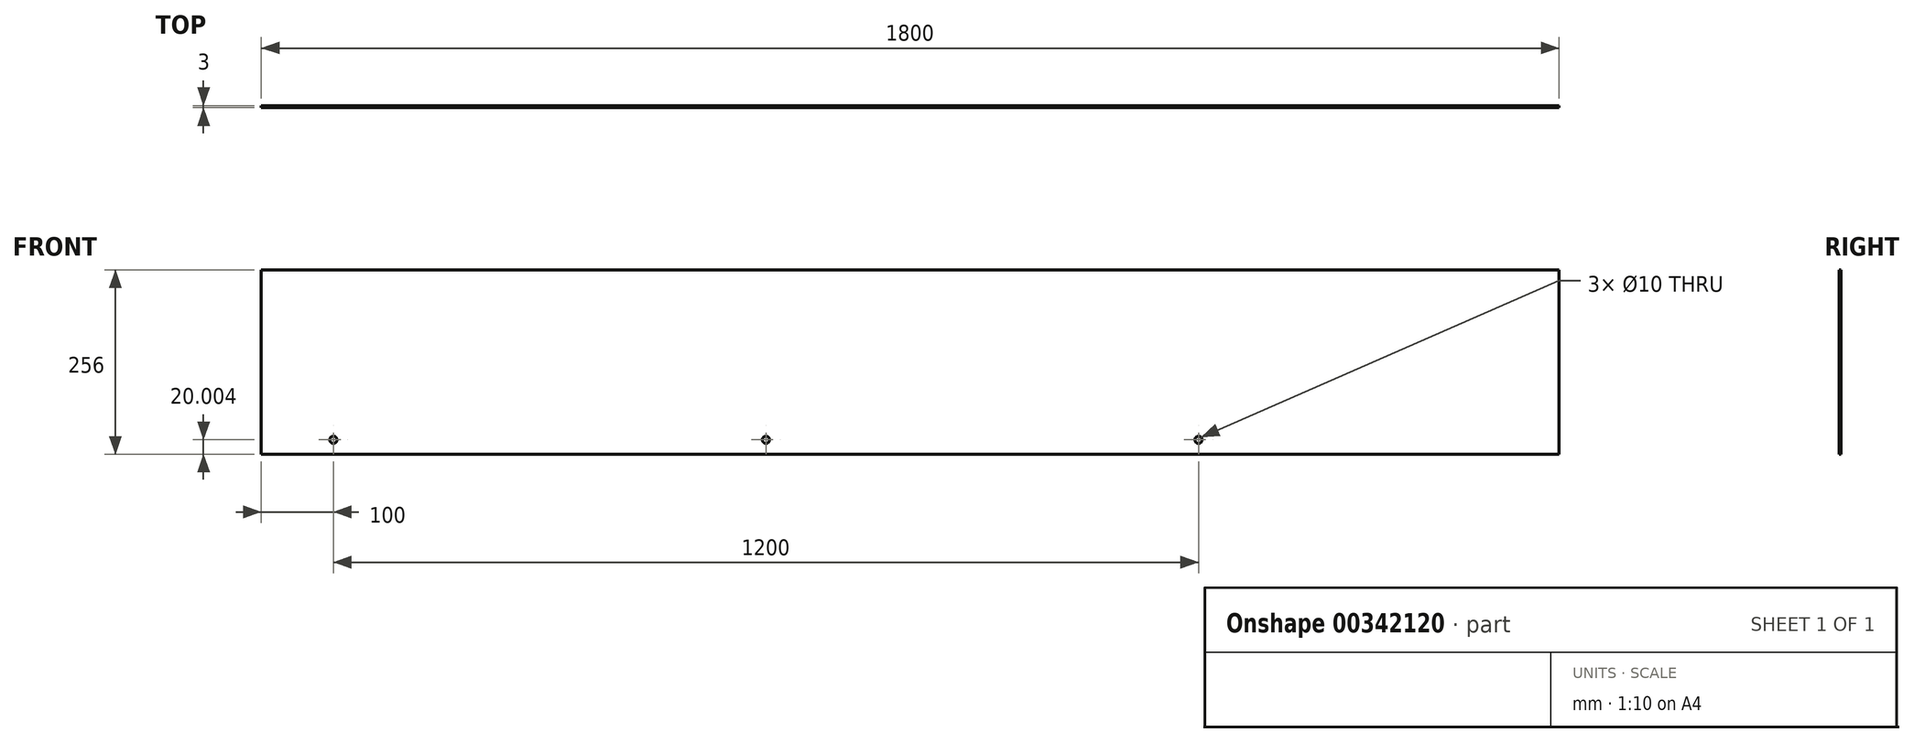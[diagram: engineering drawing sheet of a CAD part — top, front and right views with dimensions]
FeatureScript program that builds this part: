
annotation { "Feature Type Name" : "Feature", "Feature Type Description" : "" }
export const myFeature = defineFeature(function(context is Context, id is Id, definition is map)
    precondition{}
    {
        {
            var Q0;
            Q0=qCreatedBy(makeId("Front.planeOp"),FACE);
            var sketch = newSketch(context, id + "F0", { "sketchPlane" : qUnion([Q0])});
            skLineSegment(sketch, "E0", {"start": v(1913.88, -0.06) * mm, "end": v(1913.88, 255.94) * mm});
            skLineSegment(sketch, "E1", {"start": v(1913.88, -0.06) * mm, "end": v(113.88, -0.06) * mm});
            skLineSegment(sketch, "E2", {"start": v(113.88, -0.06) * mm, "end": v(113.88, 255.94) * mm});
            skLineSegment(sketch, "E3", {"start": v(113.88, 255.94) * mm, "end": v(1913.88, 255.94) * mm});
            skLineSegment(sketch, "E4", {"start": v(1913.88, 19.94) * mm, "end": v(1413.88, 19.94) * mm, "construction": true});
            skCircle(sketch, "E5", {"center": v(1413.88, 19.94) * mm, "radius": 5 * mm});
            skCircle(sketch, "E6", {"center": v(213.88, 19.94) * mm, "radius": 5 * mm});
            skCircle(sketch, "E7", {"center": v(813.88, 19.94) * mm, "radius": 5 * mm});
            skLineSegment(sketch, "E8", {"start": v(1013.88, -0.06) * mm, "end": v(1013.88, 61.63) * mm, "construction": true});
            skSolve(sketch);
        }
        {
            var Q0;
            Q0=qSketchRegion(id+"F0",true);
            extrude(context, id + "F1", {"entities" : qUnion([Q0]), "depth" : 3 * mm});
        }
    });
